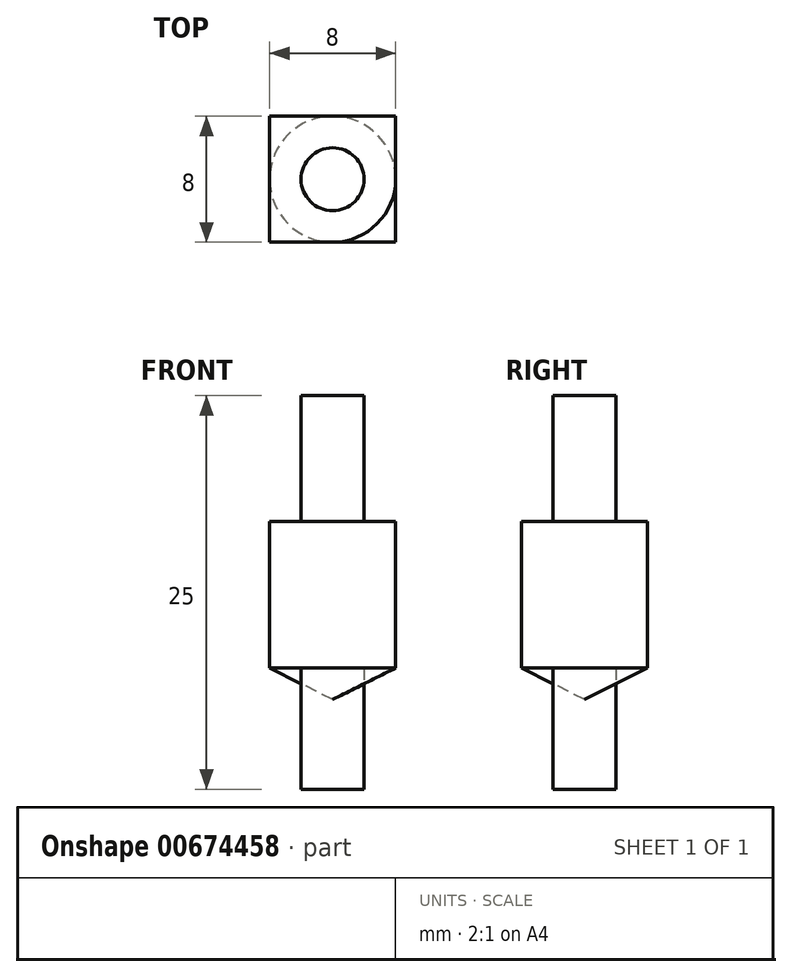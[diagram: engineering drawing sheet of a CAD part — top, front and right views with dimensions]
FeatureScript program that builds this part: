
annotation { "Feature Type Name" : "Feature", "Feature Type Description" : "" }
export const myFeature = defineFeature(function(context is Context, id is Id, definition is map)
    precondition{}
    {
        {
            var Q0;
            Q0=qCreatedBy(makeId("Top.planeOp"),FACE);
            var sketch = newSketch(context, id + "F0", { "sketchPlane" : qUnion([Q0])});
            skCircle(sketch, "E0", {"center": v(0, 0) * mm, "radius": 2 * mm});
            skSolve(sketch);
        }
        {
            var Q0;
            Q0=makeQuery(id+"F0.imprint","IMPRINT",FACE,{"disambiguationData":[TD([[makeQuery(id+"F0.imprint","IMPRINT",EDGE,{"derivedFrom":sQuery(id+"F0.wireOp",EDGE,"E0")}),1.0]])]});
            extrude(context, id + "F1", {"entities" : qUnion([Q0]), "depth" : 25 * mm, "offsetDistance" : 25 * mm});
        }
        {
            var Q0;
            Q0=makeQuery(id+"F1.opExtrude","CAP_FACE",FACE,{"disambiguationData":[OSD([sQuery(id+"F0.wireOp",EDGE,"E0")])],"isStart":false});
            cPlane(context, id + "F2", {"entities" : qUnion([Q0]), "cplaneType" : CPlaneType.OFFSET, "offset" : 8 * mm, "oppositeDirection" : true, "width" : 150 * mm, "height" : 150 * mm});
        }
        {
            var Q0;
            Q0=qCreatedBy(id+"F2.planeOp",FACE);
            var sketch = newSketch(context, id + "F3", { "sketchPlane" : qUnion([Q0])});
            skLineSegment(sketch, "E1.bottom", {"start": v(4, 4) * mm, "end": v(-4, 4) * mm});
            skLineSegment(sketch, "E1.top", {"start": v(4, -4) * mm, "end": v(-4, -4) * mm});
            skLineSegment(sketch, "E1.left", {"start": v(4, 4) * mm, "end": v(4, -4) * mm});
            skLineSegment(sketch, "E1.right", {"start": v(-4, 4) * mm, "end": v(-4, -4) * mm});
            skPoint(sketch, "E1.middle", {"position": v(0, 0) * mm});
            skSolve(sketch);
        }
        {
            var Q0;
            Q0 = qSketchRegion(id + "F3", true);
            extrude(context, id + "F4", {"entities" : qUnion([Q0]), "operationType" : NewBodyOperationType.ADD, "oppositeDirection" : true, "depth" : 9.3 * mm, "offsetDistance" : 25 * mm});
        }
        {
            var Q0;
            Q0=qCreatedBy(makeId("Front.planeOp"),FACE);
            var sketch = newSketch(context, id + "F5", { "sketchPlane" : qUnion([Q0])});
            skLineSegment(sketch, "E2", {"start": v(0, 5.7) * mm, "end": v(0, 7.7) * mm});
            skLineSegment(sketch, "E3", {"start": v(0, 7.7) * mm, "end": v(4, 7.7) * mm});
            skLineSegment(sketch, "E4", {"start": v(0, 7.7) * mm, "end": v(0, 5.7) * mm});
            skLineSegment(sketch, "E5", {"start": v(0, 5.7) * mm, "end": v(4, 7.7) * mm});
            skPoint(sketch, "E6.orphan", {"position": v(0, 0) * mm});
            skSolve(sketch);
        }
        {
            var Q0;
            Q0 = qSketchRegion(id + "F5", true);
            var Q1;
            Q1=sQuery(id+"F5.wireOp",EDGE,"E4");
            revolve(context, id + "F6", {"entities" : qUnion([Q0]), "axis" : qUnion([Q1]), "revolveType" : RevolveType.FULL});
        }
    });
